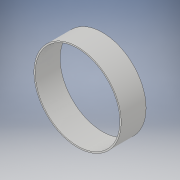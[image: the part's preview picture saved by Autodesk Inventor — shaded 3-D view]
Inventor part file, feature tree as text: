
AUTODESK INVENTOR PART (.ipt)
format: ipt  version: 2019 (Build 230136000, 136)  size: 104,448 bytes
history: native  units: mm
features: extrude x2, sketch x2
ambient origin geometry x8: Origin, YZ Plane, XZ Plane, XY Plane, X Axis, Y Axis, Z Axis, Center Point
bodies: Solid1 (feature_tree)
feature tree (4):
  extrude  "Extrusion1"  Depth=1.9mm TaperAngle=0.0deg
  extrude  "Extrusion2"  Depth=1.9mm TaperAngle=0.0deg
  sketch  "Sketch1"  dims[d0=6.66mm d1=1.9mm d2=0.0mm]
  sketch  "Sketch2"  dims[d3=6.46mm d4=1.9mm d5=0.0mm]
